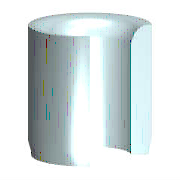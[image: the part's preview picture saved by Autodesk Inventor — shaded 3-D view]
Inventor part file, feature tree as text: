
AUTODESK INVENTOR PART (.ipt)
format: ipt  version: 2023.3 (Build 273359000, 359)  size: 153,088 bytes
history: native  units: mm (DEFAULTED — no unit token found)
features: hole x2, other x1, sketch x1
ambient origin geometry x8: Origin, YZ Plane, XZ Plane, XY Plane, X Axis, Y Axis, Z Axis, Center Point
bodies: Solid1 (feature_tree)
feature tree (4):
  other  "Körper"
  sketch  "Skizze2"  dims[d0=6.0mm d1=3.0mm d2=12.0mm d3=90.0deg d6=1.0mm d7=15.0deg d9=0.0mm d11=1.0mm d12=0.0mm d13=1.0mm d14=5.5mm d15=0.5mm d16=6.0mm d17=4.0mm d18=2.0mm d19=90.0deg d20=12.0mm d21=0.0mm d23=1.0mm d24=6.0mm d25=4.0mm d26=2.0mm d27=90.0deg d28=8.0mm d29=0.0mm d30=1.5mm]
  hole  "Bohrung1"  [1 undecoded]
  hole  "Bohrung2"  [1 undecoded]
note: 2 required parameter values undecoded (feature->parameter linkage not recoverable at this tier; creation-order binding heuristic only, values carry confidence <= 0.55)
